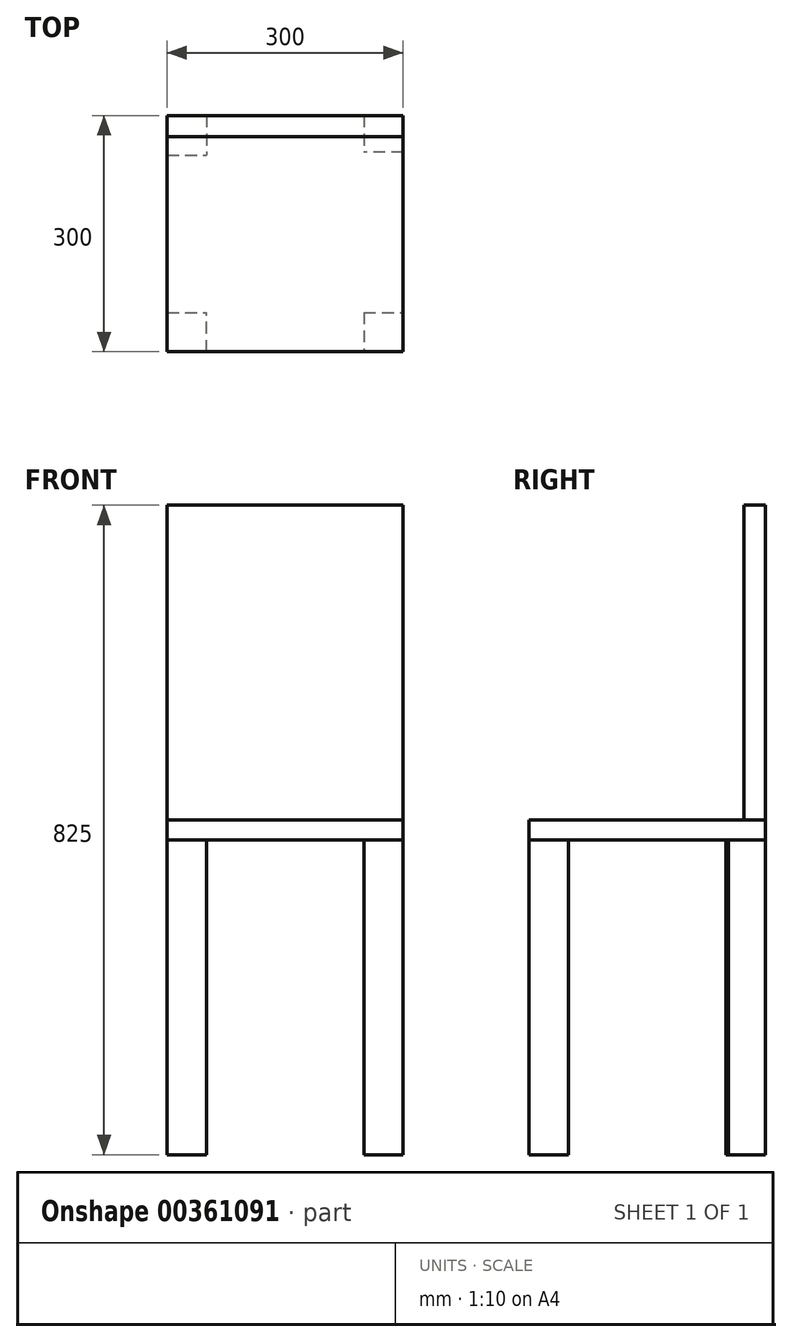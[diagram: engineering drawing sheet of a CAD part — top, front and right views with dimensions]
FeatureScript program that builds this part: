
annotation { "Feature Type Name" : "Feature", "Feature Type Description" : "" }
export const myFeature = defineFeature(function(context is Context, id is Id, definition is map)
    precondition{}
    {
        {
            var Q0;
            Q0=qCreatedBy(makeId("Top.planeOp"),FACE);
            var sketch = newSketch(context, id + "F0", { "sketchPlane" : qUnion([Q0])});
            skLineSegment(sketch, "E0.bottom", {"start": v(174.64, 150.67) * mm, "end": v(-125.36, 150.67) * mm});
            skLineSegment(sketch, "E0.top", {"start": v(174.64, -149.33) * mm, "end": v(-125.36, -149.33) * mm});
            skLineSegment(sketch, "E0.left", {"start": v(174.64, 150.67) * mm, "end": v(174.64, -149.33) * mm});
            skLineSegment(sketch, "E0.right", {"start": v(-125.36, 150.67) * mm, "end": v(-125.36, -149.33) * mm});
            skSolve(sketch);
        }
        {
            var Q0;
            Q0=makeQuery(id+"F0.imprint","IMPRINT",FACE,{"disambiguationData":[TD([[makeQuery(id+"F0.imprint","IMPRINT",EDGE,{"derivedFrom":sQuery(id+"F0.wireOp",EDGE,"E0.bottom")}),1.0]])]});
            extrude(context, id + "F1", {"entities" : qUnion([Q0]), "depth" : 25 * mm});
        }
        {
            var Q0;
            Q0=makeQuery(id+"F1.opExtrude","CAP_FACE",FACE,{"disambiguationData":[OSD([sQuery(id+"F0.wireOp",EDGE,"E0.bottom"),sQuery(id+"F0.wireOp",EDGE,"E0.top"),sQuery(id+"F0.wireOp",EDGE,"E0.left"),sQuery(id+"F0.wireOp",EDGE,"E0.right")])],"isStart":true});
            var sketch = newSketch(context, id + "F2", { "sketchPlane" : qUnion([Q0])});
            skLineSegment(sketch, "E1.bottom", {"start": v(124.64, 99.33) * mm, "end": v(174.64, 99.33) * mm});
            skLineSegment(sketch, "E1.top", {"start": v(124.64, 149.33) * mm, "end": v(174.64, 149.33) * mm});
            skLineSegment(sketch, "E1.left", {"start": v(124.64, 99.33) * mm, "end": v(124.64, 149.33) * mm});
            skLineSegment(sketch, "E1.right", {"start": v(174.64, 99.33) * mm, "end": v(174.64, 149.33) * mm});
            skLineSegment(sketch, "E2.bottom", {"start": v(-125.36, 149.33) * mm, "end": v(-75.36, 149.33) * mm});
            skLineSegment(sketch, "E2.top", {"start": v(-125.36, 99.33) * mm, "end": v(-75.36, 99.33) * mm});
            skLineSegment(sketch, "E2.left", {"start": v(-125.36, 149.33) * mm, "end": v(-125.36, 99.33) * mm});
            skLineSegment(sketch, "E2.right", {"start": v(-75.36, 149.33) * mm, "end": v(-75.36, 99.33) * mm});
            skLineSegment(sketch, "E3.bottom", {"start": v(-125.36, -150.67) * mm, "end": v(-75.36, -150.67) * mm});
            skLineSegment(sketch, "E3.top", {"start": v(-125.36, -100.67) * mm, "end": v(-75.36, -100.67) * mm});
            skLineSegment(sketch, "E3.left", {"start": v(-125.36, -150.67) * mm, "end": v(-125.36, -100.67) * mm});
            skLineSegment(sketch, "E3.right", {"start": v(-75.36, -150.67) * mm, "end": v(-75.36, -100.67) * mm});
            skLineSegment(sketch, "E4.bottom", {"start": v(174.64, -150.67) * mm, "end": v(124.64, -150.67) * mm});
            skLineSegment(sketch, "E4.top", {"start": v(174.64, -103.92) * mm, "end": v(124.64, -103.92) * mm});
            skLineSegment(sketch, "E4.left", {"start": v(174.64, -150.67) * mm, "end": v(174.64, -103.92) * mm});
            skLineSegment(sketch, "E4.right", {"start": v(124.64, -150.67) * mm, "end": v(124.64, -103.92) * mm});
            skSolve(sketch);
        }
        {
            var Q0;
            Q0=makeQuery(id+"F2.imprint","IMPRINT",FACE,{"disambiguationData":[TD([[makeQuery(id+"F2.imprint","IMPRINT",EDGE,{"derivedFrom":sQuery(id+"F2.wireOp",EDGE,"E1.bottom")}),1.0]])]});
            var Q1;
            Q1=makeQuery(id+"F2.imprint","IMPRINT",FACE,{"disambiguationData":[TD([[makeQuery(id+"F2.imprint","IMPRINT",EDGE,{"derivedFrom":sQuery(id+"F2.wireOp",EDGE,"E2.bottom")}),1.0]])]});
            var Q2;
            Q2=makeQuery(id+"F2.imprint","IMPRINT",FACE,{"disambiguationData":[TD([[makeQuery(id+"F2.imprint","IMPRINT",EDGE,{"derivedFrom":sQuery(id+"F2.wireOp",EDGE,"E3.bottom")}),-1.0]])]});
            var Q3;
            Q3=makeQuery(id+"F2.imprint","IMPRINT",FACE,{"disambiguationData":[TD([[makeQuery(id+"F2.imprint","IMPRINT",EDGE,{"derivedFrom":sQuery(id+"F2.wireOp",EDGE,"E4.bottom")}),-1.0]])]});
            extrude(context, id + "F3", {"entities" : qUnion([Q0, Q1, Q2, Q3]), "depth" : 400 * mm});
        }
        {
            var Q0;
            Q0=makeQuery(id+"F1.opExtrude","CAP_FACE",FACE,{"disambiguationData":[OSD([sQuery(id+"F0.wireOp",EDGE,"E0.bottom"),sQuery(id+"F0.wireOp",EDGE,"E0.top"),sQuery(id+"F0.wireOp",EDGE,"E0.left"),sQuery(id+"F0.wireOp",EDGE,"E0.right")])],"isStart":false});
            var sketch = newSketch(context, id + "F4", { "sketchPlane" : qUnion([Q0])});
            skLineSegment(sketch, "E5.bottom", {"start": v(174.64, 150.67) * mm, "end": v(-125.36, 150.67) * mm});
            skLineSegment(sketch, "E5.top", {"start": v(174.64, 123.78) * mm, "end": v(-125.36, 123.78) * mm});
            skLineSegment(sketch, "E5.left", {"start": v(174.64, 150.67) * mm, "end": v(174.64, 123.78) * mm});
            skLineSegment(sketch, "E5.right", {"start": v(-125.36, 150.67) * mm, "end": v(-125.36, 123.78) * mm});
            skSolve(sketch);
        }
        {
            var Q0;
            Q0=makeQuery(id+"F4.imprint","IMPRINT",FACE,{"disambiguationData":[TD([[makeQuery(id+"F4.imprint","IMPRINT",EDGE,{"derivedFrom":sQuery(id+"F4.wireOp",EDGE,"E5.bottom")}),1.0]])]});
            extrude(context, id + "F5", {"entities" : qUnion([Q0]), "depth" : 400 * mm});
        }
    });
